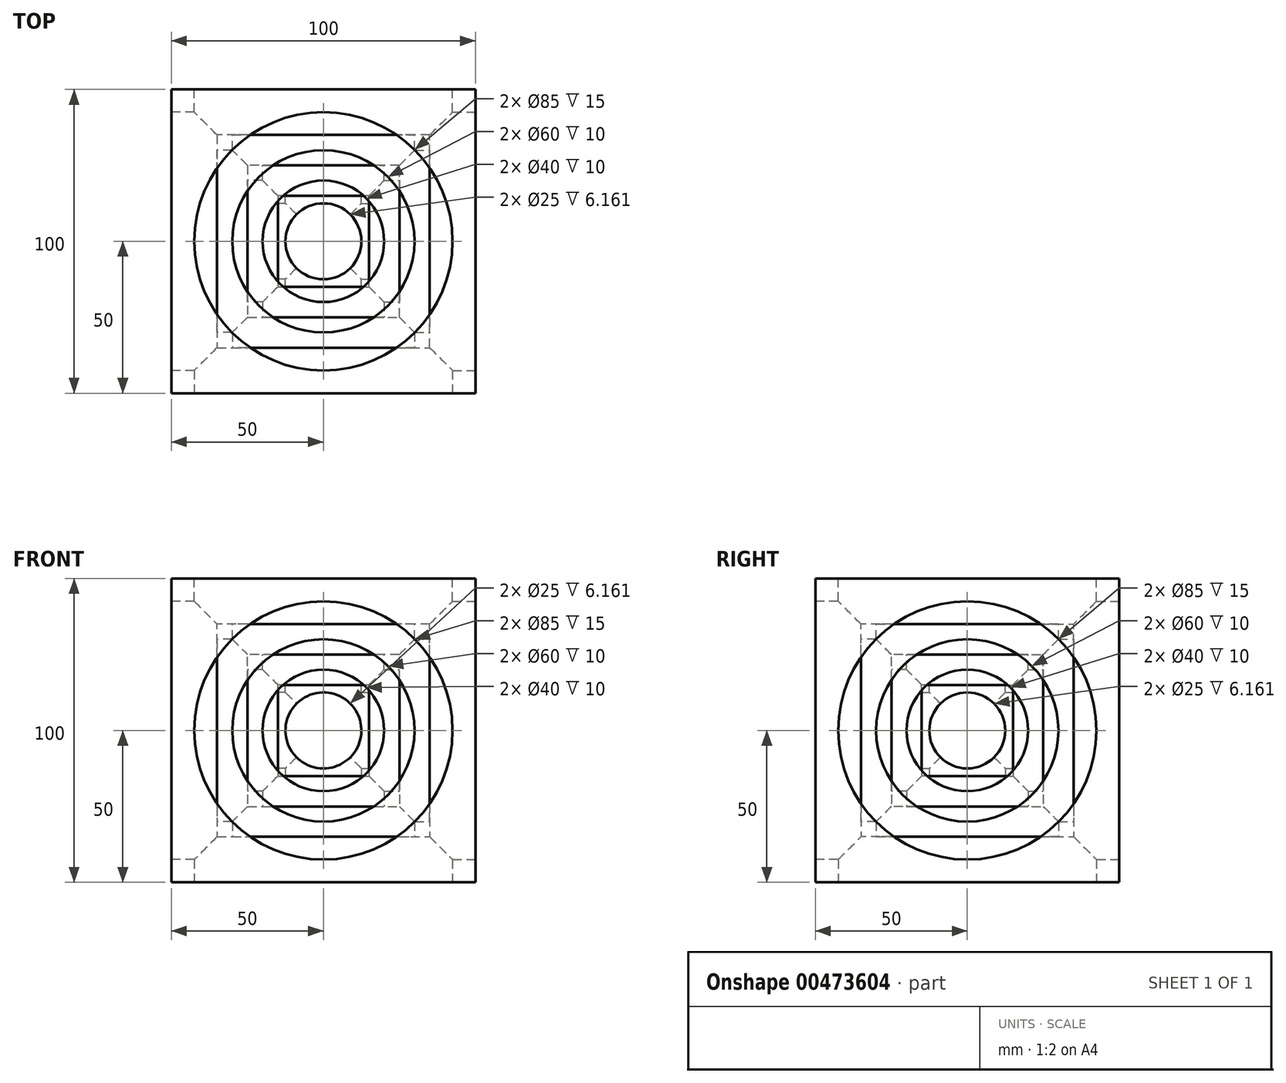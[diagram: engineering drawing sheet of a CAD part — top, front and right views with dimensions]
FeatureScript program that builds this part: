
annotation { "Feature Type Name" : "Feature", "Feature Type Description" : "" }
export const myFeature = defineFeature(function(context is Context, id is Id, definition is map)
    precondition{}
    {
        {
            var Q0;
            Q0=qCreatedBy(makeId("Front.planeOp"),FACE);
            var sketch = newSketch(context, id + "F0", { "sketchPlane" : qUnion([Q0])});
            skLineSegment(sketch, "E0.bottom", {"start": v(-50, 50) * mm, "end": v(50, 50) * mm});
            skLineSegment(sketch, "E0.top", {"start": v(-50, -50) * mm, "end": v(50, -50) * mm});
            skLineSegment(sketch, "E0.left", {"start": v(-50, 50) * mm, "end": v(-50, -50) * mm});
            skLineSegment(sketch, "E0.right", {"start": v(50, 50) * mm, "end": v(50, -50) * mm});
            skSolve(sketch);
        }
        {
            var Q0;
            Q0=makeQuery(id+"F0.imprint","IMPRINT",FACE,{"disambiguationData":[TD([[makeQuery(id+"F0.imprint","IMPRINT",EDGE,{"derivedFrom":sQuery(id+"F0.wireOp",EDGE,"E0.bottom")}),-1.0]])]});
            extrude(context, id + "F1", {"entities" : qUnion([Q0]), "endBound" : BoundingType.SYMMETRIC, "depth" : 100 * mm});
        }
        {
            var Q0;
            Q0=makeQuery(id+"F1.opExtrude","SWEPT_FACE",FACE,{"disambiguationData":[OSD([sQuery(id+"F0.wireOp",EDGE,"E0.right")])]});
            var sketch = newSketch(context, id + "F2", { "sketchPlane" : qUnion([Q0])});
            skCircle(sketch, "E1", {"center": v(0, 0) * mm, "radius": 42.5 * mm});
            skSolve(sketch);
        }
        {
            var Q0;
            Q0=makeQuery(id+"F2.imprint","IMPRINT",FACE,{"disambiguationData":[TD([[makeQuery(id+"F2.imprint","IMPRINT",EDGE,{"derivedFrom":sQuery(id+"F2.wireOp",EDGE,"E1")}),1.0]])]});
            extrude(context, id + "F3", {"entities" : qUnion([Q0]), "operationType" : NewBodyOperationType.REMOVE, "oppositeDirection" : true, "depth" : 15 * mm});
        }
        {
            var Q0;
            Q0=makeQuery(id+"F1.opExtrude","CAP_FACE",FACE,{"disambiguationData":[OSD([sQuery(id+"F0.wireOp",EDGE,"E0.bottom"),sQuery(id+"F0.wireOp",EDGE,"E0.top"),sQuery(id+"F0.wireOp",EDGE,"E0.left"),sQuery(id+"F0.wireOp",EDGE,"E0.right")])],"isStart":false});
            var sketch = newSketch(context, id + "F4", { "sketchPlane" : qUnion([Q0])});
            skCircle(sketch, "E2", {"center": v(0, 0) * mm, "radius": 42.5 * mm});
            skSolve(sketch);
        }
        {
            var Q0;
            Q0=makeQuery(id+"F4.imprint","IMPRINT",FACE,{"disambiguationData":[TD([[makeQuery(id+"F4.imprint","IMPRINT",EDGE,{"derivedFrom":sQuery(id+"F4.wireOp",EDGE,"E2")}),1.0]])]});
            extrude(context, id + "F5", {"entities" : qUnion([Q0]), "operationType" : NewBodyOperationType.REMOVE, "oppositeDirection" : true, "depth" : 15 * mm});
        }
        {
            var Q0;
            Q0=makeQuery(id+"F1.opExtrude","SWEPT_FACE",FACE,{"disambiguationData":[OSD([sQuery(id+"F0.wireOp",EDGE,"E0.left")])]});
            var sketch = newSketch(context, id + "F6", { "sketchPlane" : qUnion([Q0])});
            skCircle(sketch, "E3", {"center": v(0, 0) * mm, "radius": 42.5 * mm});
            skSolve(sketch);
        }
        {
            var Q0;
            Q0 = qSketchRegion(id + "F6", true);
            extrude(context, id + "F7", {"entities" : qUnion([Q0]), "operationType" : NewBodyOperationType.REMOVE, "oppositeDirection" : true, "depth" : 15 * mm});
        }
        {
            var Q0;
            Q0=makeQuery(id+"F1.opExtrude","CAP_FACE",FACE,{"disambiguationData":[OSD([sQuery(id+"F0.wireOp",EDGE,"E0.bottom"),sQuery(id+"F0.wireOp",EDGE,"E0.top"),sQuery(id+"F0.wireOp",EDGE,"E0.left"),sQuery(id+"F0.wireOp",EDGE,"E0.right")])],"isStart":true});
            var sketch = newSketch(context, id + "F8", { "sketchPlane" : qUnion([Q0])});
            skCircle(sketch, "E4", {"center": v(0, 0) * mm, "radius": 42.5 * mm});
            skSolve(sketch);
        }
        {
            var Q0;
            Q0 = qSketchRegion(id + "F8", true);
            extrude(context, id + "F9", {"entities" : qUnion([Q0]), "operationType" : NewBodyOperationType.REMOVE, "oppositeDirection" : true, "depth" : 15 * mm});
        }
        {
            var Q0;
            Q0=makeQuery(id+"F5.boolean.opBoolean","COPY",FACE,{"derivedFrom":makeQuery(id+"F5.opExtrude","CAP_FACE",FACE,{"disambiguationData":[OSD([sQuery(id+"F4.wireOp",EDGE,"E2")])],"isStart":false})});
            var sketch = newSketch(context, id + "F10", { "sketchPlane" : qUnion([Q0])});
            skCircle(sketch, "E5", {"center": v(0, 0) * mm, "radius": 30 * mm});
            skSolve(sketch);
        }
        {
            var Q0;
            Q0 = qSketchRegion(id + "F10", true);
            extrude(context, id + "F11", {"entities" : qUnion([Q0]), "operationType" : NewBodyOperationType.REMOVE, "oppositeDirection" : true, "depth" : 10 * mm});
        }
        {
            var Q0;
            Q0=makeQuery(id+"F7.boolean.opBoolean","COPY",FACE,{"derivedFrom":makeQuery(id+"F7.opExtrude","CAP_FACE",FACE,{"disambiguationData":[OSD([sQuery(id+"F6.wireOp",EDGE,"E3")])],"isStart":false})});
            var sketch = newSketch(context, id + "F12", { "sketchPlane" : qUnion([Q0])});
            skCircle(sketch, "E6", {"center": v(0, 0) * mm, "radius": 30 * mm});
            skSolve(sketch);
        }
        {
            var Q0;
            Q0 = qSketchRegion(id + "F12", true);
            extrude(context, id + "F13", {"entities" : qUnion([Q0]), "operationType" : NewBodyOperationType.REMOVE, "oppositeDirection" : true, "depth" : 10 * mm});
        }
        {
            var Q0;
            Q0=makeQuery(id+"F9.boolean.opBoolean","COPY",FACE,{"derivedFrom":makeQuery(id+"F9.opExtrude","CAP_FACE",FACE,{"disambiguationData":[OSD([sQuery(id+"F8.wireOp",EDGE,"E4")])],"isStart":false})});
            var sketch = newSketch(context, id + "F14", { "sketchPlane" : qUnion([Q0])});
            skCircle(sketch, "E7", {"center": v(0, 0) * mm, "radius": 30 * mm});
            skSolve(sketch);
        }
        {
            var Q0;
            Q0 = qSketchRegion(id + "F14", true);
            extrude(context, id + "F15", {"entities" : qUnion([Q0]), "operationType" : NewBodyOperationType.REMOVE, "oppositeDirection" : true, "depth" : 10 * mm});
        }
        {
            var Q0;
            Q0=makeQuery(id+"F3.boolean.opBoolean","COPY",FACE,{"derivedFrom":makeQuery(id+"F3.opExtrude","CAP_FACE",FACE,{"disambiguationData":[OSD([sQuery(id+"F2.wireOp",EDGE,"E1")])],"isStart":false})});
            var sketch = newSketch(context, id + "F16", { "sketchPlane" : qUnion([Q0])});
            skCircle(sketch, "E8", {"center": v(0, 0) * mm, "radius": 30 * mm});
            skSolve(sketch);
        }
        {
            var Q0;
            Q0 = qSketchRegion(id + "F16", true);
            extrude(context, id + "F17", {"entities" : qUnion([Q0]), "operationType" : NewBodyOperationType.REMOVE, "oppositeDirection" : true, "depth" : 10 * mm});
        }
        {
            var Q0;
            Q0=makeQuery(id+"F17.boolean.opBoolean","COPY",FACE,{"derivedFrom":makeQuery(id+"F17.opExtrude","CAP_FACE",FACE,{"disambiguationData":[OSD([sQuery(id+"F16.wireOp",EDGE,"E8")])],"isStart":false})});
            var sketch = newSketch(context, id + "F18", { "sketchPlane" : qUnion([Q0])});
            skCircle(sketch, "E9", {"center": v(0, 0) * mm, "radius": 20 * mm});
            skSolve(sketch);
        }
        {
            var Q0;
            Q0 = qSketchRegion(id + "F18", true);
            extrude(context, id + "F19", {"entities" : qUnion([Q0]), "operationType" : NewBodyOperationType.REMOVE, "oppositeDirection" : true, "depth" : 10 * mm});
        }
        {
            var Q0;
            Q0=makeQuery(id+"F11.boolean.opBoolean","COPY",FACE,{"derivedFrom":makeQuery(id+"F11.opExtrude","CAP_FACE",FACE,{"disambiguationData":[OSD([sQuery(id+"F10.wireOp",EDGE,"E5")])],"isStart":false})});
            var sketch = newSketch(context, id + "F20", { "sketchPlane" : qUnion([Q0])});
            skCircle(sketch, "E10", {"center": v(0, 0) * mm, "radius": 20 * mm});
            skSolve(sketch);
        }
        {
            var Q0;
            Q0 = qSketchRegion(id + "F20", true);
            extrude(context, id + "F21", {"entities" : qUnion([Q0]), "operationType" : NewBodyOperationType.REMOVE, "oppositeDirection" : true, "depth" : 10 * mm});
        }
        {
            var Q0;
            Q0=makeQuery(id+"F13.boolean.opBoolean","COPY",FACE,{"derivedFrom":makeQuery(id+"F13.opExtrude","CAP_FACE",FACE,{"disambiguationData":[OSD([sQuery(id+"F12.wireOp",EDGE,"E6")])],"isStart":false})});
            var sketch = newSketch(context, id + "F22", { "sketchPlane" : qUnion([Q0])});
            skCircle(sketch, "E11", {"center": v(0, 0) * mm, "radius": 20 * mm});
            skSolve(sketch);
        }
        {
            var Q0;
            Q0 = qSketchRegion(id + "F22", true);
            extrude(context, id + "F23", {"entities" : qUnion([Q0]), "operationType" : NewBodyOperationType.REMOVE, "oppositeDirection" : true, "depth" : 10 * mm});
        }
        {
            var Q0;
            Q0=makeQuery(id+"F15.boolean.opBoolean","COPY",FACE,{"derivedFrom":makeQuery(id+"F15.opExtrude","CAP_FACE",FACE,{"disambiguationData":[OSD([sQuery(id+"F14.wireOp",EDGE,"E7")])],"isStart":false})});
            var sketch = newSketch(context, id + "F24", { "sketchPlane" : qUnion([Q0])});
            skCircle(sketch, "E12", {"center": v(0, 0) * mm, "radius": 20 * mm});
            skSolve(sketch);
        }
        {
            var Q0;
            Q0 = qSketchRegion(id + "F24", true);
            extrude(context, id + "F25", {"entities" : qUnion([Q0]), "operationType" : NewBodyOperationType.REMOVE, "oppositeDirection" : true, "depth" : 10 * mm});
        }
        {
            var Q0;
            Q0=makeQuery(id+"F25.boolean.opBoolean","COPY",FACE,{"derivedFrom":makeQuery(id+"F25.opExtrude","CAP_FACE",FACE,{"disambiguationData":[OSD([sQuery(id+"F24.wireOp",EDGE,"E12")])],"isStart":false})});
            var sketch = newSketch(context, id + "F26", { "sketchPlane" : qUnion([Q0])});
            skCircle(sketch, "E13", {"center": v(0, 0) * mm, "radius": 12.5 * mm});
            skSolve(sketch);
        }
        {
            var Q0;
            Q0 = qSketchRegion(id + "F26", true);
            extrude(context, id + "F27", {"entities" : qUnion([Q0]), "operationType" : NewBodyOperationType.REMOVE, "oppositeDirection" : true, "depth" : 10 * mm});
        }
        {
            var Q0;
            Q0=makeQuery(id+"F19.boolean.opBoolean","COPY",FACE,{"derivedFrom":makeQuery(id+"F19.opExtrude","CAP_FACE",FACE,{"disambiguationData":[OSD([sQuery(id+"F18.wireOp",EDGE,"E9")])],"isStart":false})});
            var sketch = newSketch(context, id + "F28", { "sketchPlane" : qUnion([Q0])});
            skCircle(sketch, "E14", {"center": v(0, 0) * mm, "radius": 12.5 * mm});
            skSolve(sketch);
        }
        {
            var Q0;
            Q0 = qSketchRegion(id + "F28", true);
            extrude(context, id + "F29", {"entities" : qUnion([Q0]), "operationType" : NewBodyOperationType.REMOVE, "oppositeDirection" : true, "depth" : 10 * mm});
        }
        {
            var Q0;
            Q0=makeQuery(id+"F21.boolean.opBoolean","COPY",FACE,{"derivedFrom":makeQuery(id+"F21.opExtrude","CAP_FACE",FACE,{"disambiguationData":[OSD([sQuery(id+"F20.wireOp",EDGE,"E10")])],"isStart":false})});
            var sketch = newSketch(context, id + "F30", { "sketchPlane" : qUnion([Q0])});
            skCircle(sketch, "E15", {"center": v(0, 0) * mm, "radius": 12.5 * mm});
            skSolve(sketch);
        }
        {
            var Q0;
            Q0 = qSketchRegion(id + "F30", true);
            extrude(context, id + "F31", {"entities" : qUnion([Q0]), "operationType" : NewBodyOperationType.REMOVE, "endBound" : BoundingType.THROUGH_ALL, "oppositeDirection" : true, "depth" : 10 * mm});
        }
        {
            var Q0;
            Q0=makeQuery(id+"F23.boolean.opBoolean","COPY",FACE,{"derivedFrom":makeQuery(id+"F23.opExtrude","CAP_FACE",FACE,{"disambiguationData":[OSD([sQuery(id+"F22.wireOp",EDGE,"E11")])],"isStart":false})});
            var sketch = newSketch(context, id + "F32", { "sketchPlane" : qUnion([Q0])});
            skCircle(sketch, "E16", {"center": v(0, 0) * mm, "radius": 12.5 * mm});
            skSolve(sketch);
        }
        {
            var Q0;
            Q0 = qSketchRegion(id + "F32", true);
            extrude(context, id + "F33", {"entities" : qUnion([Q0]), "operationType" : NewBodyOperationType.REMOVE, "endBound" : BoundingType.THROUGH_ALL, "oppositeDirection" : true, "depth" : 10 * mm});
        }
        {
            var Q0;
            Q0=makeQuery(id+"F1.opExtrude","SWEPT_FACE",FACE,{"disambiguationData":[OSD([sQuery(id+"F0.wireOp",EDGE,"E0.bottom")])]});
            var sketch = newSketch(context, id + "F34", { "sketchPlane" : qUnion([Q0])});
            skCircle(sketch, "E17", {"center": v(0, 0) * mm, "radius": 42.5 * mm});
            skSolve(sketch);
        }
        {
            var Q0;
            Q0 = qSketchRegion(id + "F34", true);
            extrude(context, id + "F35", {"entities" : qUnion([Q0]), "operationType" : NewBodyOperationType.REMOVE, "oppositeDirection" : true, "depth" : 15 * mm});
        }
        {
            var Q0;
            Q0=makeQuery(id+"F35.boolean.opBoolean","COPY",FACE,{"derivedFrom":makeQuery(id+"F35.opExtrude","CAP_FACE",FACE,{"disambiguationData":[OSD([sQuery(id+"F34.wireOp",EDGE,"E17")])],"isStart":false})});
            var sketch = newSketch(context, id + "F36", { "sketchPlane" : qUnion([Q0])});
            skCircle(sketch, "E18", {"center": v(0, 0) * mm, "radius": 30 * mm});
            skSolve(sketch);
        }
        {
            var Q0;
            Q0 = qSketchRegion(id + "F36", true);
            extrude(context, id + "F37", {"entities" : qUnion([Q0]), "operationType" : NewBodyOperationType.REMOVE, "oppositeDirection" : true, "depth" : 10 * mm});
        }
        {
            var Q0;
            Q0=makeQuery(id+"F37.boolean.opBoolean","COPY",FACE,{"derivedFrom":makeQuery(id+"F37.opExtrude","CAP_FACE",FACE,{"disambiguationData":[OSD([sQuery(id+"F36.wireOp",EDGE,"E18")])],"isStart":false})});
            var sketch = newSketch(context, id + "F38", { "sketchPlane" : qUnion([Q0])});
            skCircle(sketch, "E19", {"center": v(0, 0) * mm, "radius": 20 * mm});
            skSolve(sketch);
        }
        {
            var Q0;
            Q0 = qSketchRegion(id + "F38", true);
            extrude(context, id + "F39", {"entities" : qUnion([Q0]), "operationType" : NewBodyOperationType.REMOVE, "oppositeDirection" : true, "depth" : 10 * mm});
        }
        {
            var Q0;
            Q0=makeQuery(id+"F39.boolean.opBoolean","COPY",FACE,{"derivedFrom":makeQuery(id+"F39.opExtrude","CAP_FACE",FACE,{"disambiguationData":[OSD([sQuery(id+"F38.wireOp",EDGE,"E19")])],"isStart":false})});
            var sketch = newSketch(context, id + "F40", { "sketchPlane" : qUnion([Q0])});
            skCircle(sketch, "E20", {"center": v(0, 0) * mm, "radius": 12.5 * mm});
            skSolve(sketch);
        }
        {
            var Q0;
            Q0 = qSketchRegion(id + "F40", true);
            extrude(context, id + "F41", {"entities" : qUnion([Q0]), "operationType" : NewBodyOperationType.REMOVE, "oppositeDirection" : true, "depth" : 10 * mm});
        }
        {
            var Q0;
            Q0=makeQuery(id+"F1.opExtrude","SWEPT_FACE",FACE,{"disambiguationData":[OSD([sQuery(id+"F0.wireOp",EDGE,"E0.top")])]});
            var sketch = newSketch(context, id + "F42", { "sketchPlane" : qUnion([Q0])});
            skCircle(sketch, "E21", {"center": v(0, 0) * mm, "radius": 42.5 * mm});
            skSolve(sketch);
        }
        {
            var Q0;
            Q0 = qSketchRegion(id + "F42", true);
            extrude(context, id + "F43", {"entities" : qUnion([Q0]), "operationType" : NewBodyOperationType.REMOVE, "oppositeDirection" : true, "depth" : 15 * mm});
        }
        {
            var Q0;
            Q0=makeQuery(id+"F43.boolean.opBoolean","COPY",FACE,{"derivedFrom":makeQuery(id+"F43.opExtrude","CAP_FACE",FACE,{"disambiguationData":[OSD([sQuery(id+"F42.wireOp",EDGE,"E21")])],"isStart":false})});
            var sketch = newSketch(context, id + "F44", { "sketchPlane" : qUnion([Q0])});
            skCircle(sketch, "E22", {"center": v(0, 0) * mm, "radius": 30 * mm});
            skSolve(sketch);
        }
        {
            var Q0;
            Q0 = qSketchRegion(id + "F44", true);
            extrude(context, id + "F45", {"entities" : qUnion([Q0]), "operationType" : NewBodyOperationType.REMOVE, "oppositeDirection" : true, "depth" : 10 * mm});
        }
        {
            var Q0;
            Q0=makeQuery(id+"F45.boolean.opBoolean","COPY",FACE,{"derivedFrom":makeQuery(id+"F45.opExtrude","CAP_FACE",FACE,{"disambiguationData":[OSD([sQuery(id+"F44.wireOp",EDGE,"E22")])],"isStart":false})});
            var sketch = newSketch(context, id + "F46", { "sketchPlane" : qUnion([Q0])});
            skCircle(sketch, "E23", {"center": v(0, 0) * mm, "radius": 20 * mm});
            skSolve(sketch);
        }
        {
            var Q0;
            Q0 = qSketchRegion(id + "F46", true);
            extrude(context, id + "F47", {"entities" : qUnion([Q0]), "operationType" : NewBodyOperationType.REMOVE, "oppositeDirection" : true, "depth" : 10 * mm});
        }
        {
            var Q0;
            Q0=makeQuery(id+"F47.boolean.opBoolean","COPY",FACE,{"derivedFrom":makeQuery(id+"F47.opExtrude","CAP_FACE",FACE,{"disambiguationData":[OSD([sQuery(id+"F46.wireOp",EDGE,"E23")])],"isStart":false})});
            var sketch = newSketch(context, id + "F48", { "sketchPlane" : qUnion([Q0])});
            skCircle(sketch, "E24", {"center": v(0, 0) * mm, "radius": 12.5 * mm});
            skSolve(sketch);
        }
        {
            var Q0;
            Q0 = qSketchRegion(id + "F48", true);
            extrude(context, id + "F49", {"entities" : qUnion([Q0]), "operationType" : NewBodyOperationType.REMOVE, "endBound" : BoundingType.THROUGH_ALL, "oppositeDirection" : true, "depth" : 25 * mm});
        }
    });
